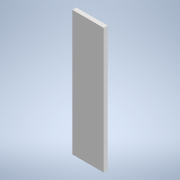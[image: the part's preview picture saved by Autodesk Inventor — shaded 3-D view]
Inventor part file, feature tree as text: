
AUTODESK INVENTOR PART (.ipt)
format: ipt  version: 2021 (Build 250183000, 183)  size: 91,648 bytes
history: native  units: in
note: dims shown in document units (in); Inventor stores cm internally (conversion verified against a paired STEP export)
features: sketch x2, extrude x1
ambient origin geometry x8: Origin, YZ Plane, XZ Plane, XY Plane, X Axis, Y Axis, Z Axis, Center Point
bodies: Solid1 (feature_tree)
feature tree (3):
  extrude  "Extrusion1"  [1 undecoded]
  sketch  "Sketch2"
  sketch  "Sketch1"  dims[d0=0.5in d1=0.0in]
note: 1 required parameter value undecoded (feature->parameter linkage not recoverable at this tier; creation-order binding heuristic only, values carry confidence <= 0.55)
